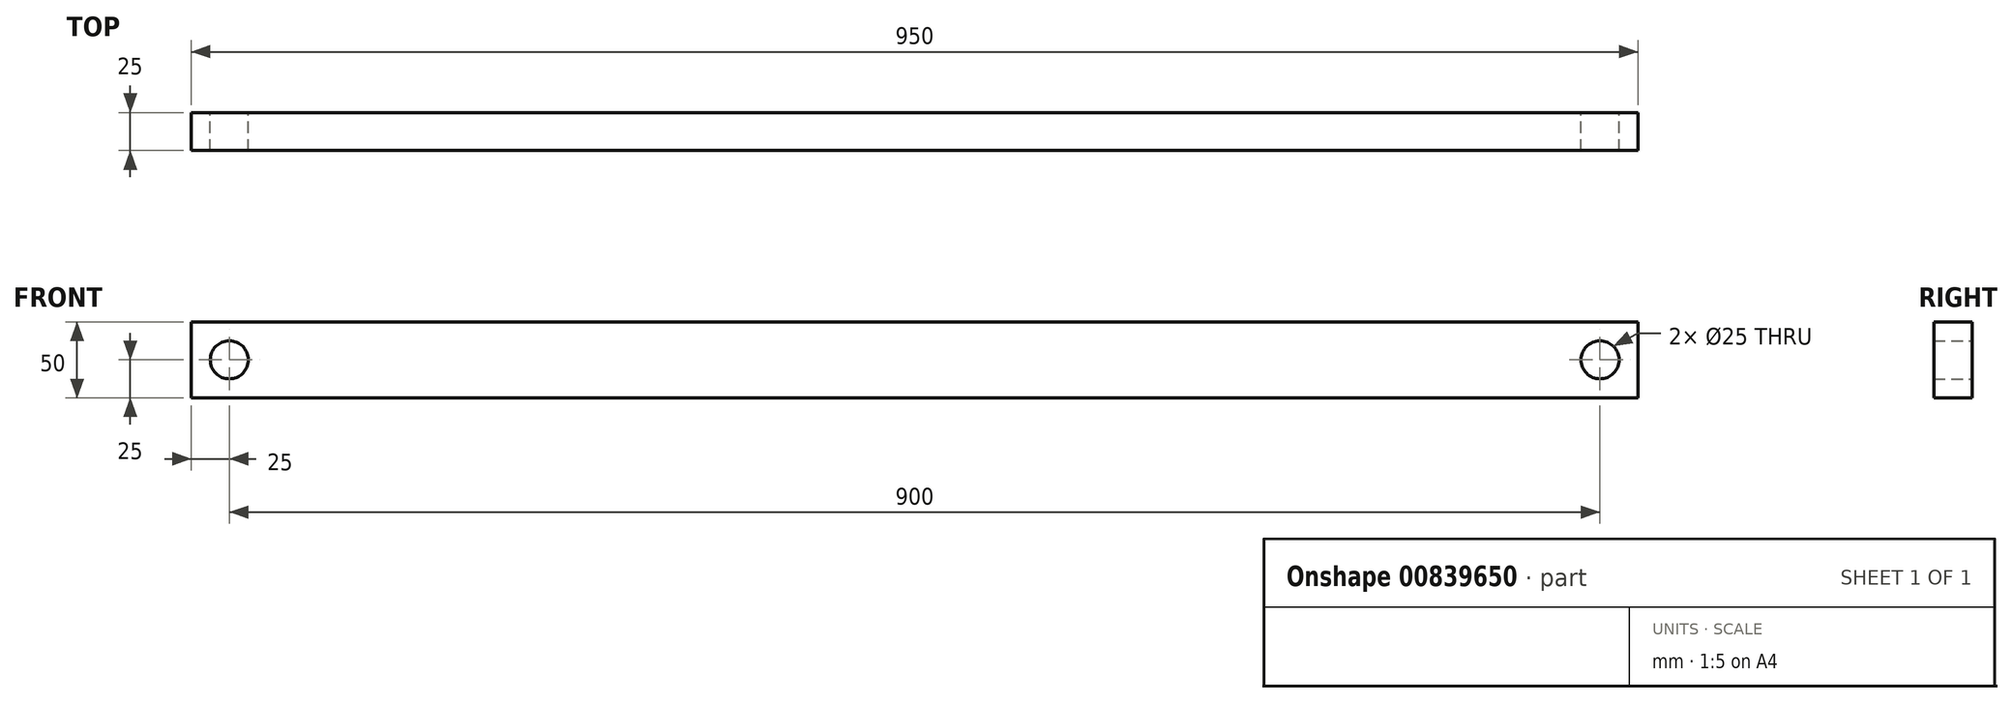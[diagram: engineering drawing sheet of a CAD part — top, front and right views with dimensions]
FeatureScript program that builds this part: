
annotation { "Feature Type Name" : "Feature", "Feature Type Description" : "" }
export const myFeature = defineFeature(function(context is Context, id is Id, definition is map)
    precondition{}
    {
        {
            var Q0;
            Q0=qCreatedBy(makeId("Front.planeOp"),FACE);
            var sketch = newSketch(context, id + "F0", { "sketchPlane" : qUnion([Q0])});
            skCircle(sketch, "E0", {"center": v(-450, 0) * mm, "radius": 12.5 * mm});
            skCircle(sketch, "E1", {"center": v(450, 0) * mm, "radius": 12.5 * mm});
            skLineSegment(sketch, "E2", {"start": v(-450, 0) * mm, "end": v(450, 0) * mm, "construction": true});
            skPoint(sketch, "E3", {"position": v(0, 0) * mm});
            skLineSegment(sketch, "E4.bottom", {"start": v(-475, 25) * mm, "end": v(475, 25) * mm});
            skLineSegment(sketch, "E4.top", {"start": v(-475, -25) * mm, "end": v(475, -25) * mm});
            skLineSegment(sketch, "E4.left", {"start": v(-475, 25) * mm, "end": v(-475, -25) * mm});
            skLineSegment(sketch, "E4.right", {"start": v(475, 25) * mm, "end": v(475, -25) * mm});
            skLineSegment(sketch, "E5", {"start": v(450, 0) * mm, "end": v(475, 25) * mm, "construction": true});
            skLineSegment(sketch, "E6", {"start": v(450, 0) * mm, "end": v(475, -25) * mm, "construction": true});
            skLineSegment(sketch, "E7", {"start": v(-450, 0) * mm, "end": v(-475, 25) * mm, "construction": true});
            skLineSegment(sketch, "E8", {"start": v(-450, 0) * mm, "end": v(-475, -25) * mm, "construction": true});
            skSolve(sketch);
        }
        {
            var Q0;
            Q0=makeQuery(id+"F0.imprint","IMPRINT",FACE,{"disambiguationData":[TD([[makeQuery(id+"F0.imprint","IMPRINT",EDGE,{"derivedFrom":sQuery(id+"F0.wireOp",EDGE,"E0")}),-1.0]])]});
            extrude(context, id + "F1", {"entities" : qUnion([Q0]), "depth" : 25 * mm, "offsetDistance" : 25 * mm});
        }
    });
